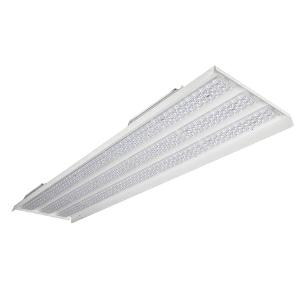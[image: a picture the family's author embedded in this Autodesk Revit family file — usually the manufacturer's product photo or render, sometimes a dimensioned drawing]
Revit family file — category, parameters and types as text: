
# Revit family: 3f_filippi_-_kit_led_retrofit_beta_430_3x_3f_filippi_-_a5311_a5322_-_kit_led_beta_430_-_l1551-_3x65w_ampio___vs_731e
name_source: partatom
category: Lighting Fixtures
units: mm (PartAtom-declared; Revit-internal decimal feet)

## family parameters
Cut with Voids When Loaded = No
Host = Face
Light Source = No
Part Type = Normal
Room Calculation Point = No
Round Connector Dimension = Use Diameter
Shared = No

## types (1)
- 3F Filippi - Kit LED Retrofit Beta 430 3X (1 x LED, 25759 lm, 173 W, 4000 K)
    Apparent Load = 173 VA
    Approval mark = ENEC
    CIE Flux Codes = 67 92 98 100 100
    Color Rendering = 80
    Color Temperature = 4000 K
    Control Gear = Electronic ballast
    Default Elevation = 1800 mm
    Description = Beta 430 Retrofit Kit to replace the 4x80W T5 Amalgam version

ILLUMINOTECHNICAL
Luminous efficiency 100% (DLOR 100%, ULOR 0%).
Initial luminous flux of the luminaire 25759 lm.
Wide symmetric distribution.
Installation Interdistance Transv.D = 1.36 x hu - Long.D = 1.35 x hu.
Tabular UGR (CIE 117 - 4H-8H; S=0.25H; 70/50/20): RUG 20.8 - 21.3.
Beam angle: 88° - 89°.
Luminous efficacy 149 lm/W.
Lifetime (L93/B10): 30000 h. (tq+25°C)
Lifetime (L90/B10): 50000 h. (tq+25°C)
Lifetime (L85/B10): 80000 h. (tq+25°C)
Lifetime (L80/B10): 100000 h. (tq+25°C)
Lifetime (L85/B10): 50000 h. (tq+40°C)
Sudden decreased luminous flux after 50000 hours: 0% (C0).
Photobiological safety in compliance with IEC/TR 62778: RG0 risk exempt, (IEC 62471).
In compliance with IEC/EN 62722-2-1 - IEC/EN 62717 standards.

SOURCE
3 linear LED modules 65W/840.
Energy efficiency class (UE 2019/2020 - UE 2019/2015): C.
CIE 13.3 Colour rendering index: CRI >80 (R9 <50%).
IES TM-30 Fidelity Index: Rf = 84 Rg = 95.
CCT nominal colour temperature 4000 K.
Colour initial tolerance (MacAdam): SDCM 3.

MECHANICAL
Gear-tray unit hot-galvanised steel, painted in white polyester.
Methacrylate (PMMA) lenses with external flat surface.
Luminaire with limited surface temperature. - D - (EN 60598-2-24)
Dimensions: 1551x430 mm, height 159 mm. Weight 13.875 kg.
Mechanical strength to impacts IK08 (5 joule).
Glow-wire test resistance 850°C.

ELECTRICAL
Halogen Free electronic wiring 230V-50/60Hz, power factor 0.97, THD <25%, constant output current, class I, 2 driver.
Twin-circuit.
Power of the luminaire 173 W.
CE - IEC 60598-1 - EN 60598-1.
SAFE FLICKER: PstLM=<1 and SVM=<0.4 (IEC TR 61547-1 and IEC TR 63158), to ensure a more comfortable and safe light.
Luminaire compliant with EN 60598-2-22 for power supply from a centralised emergency system CPSS (Central Power Supply System), not incorporated in the luminaire - high risk areas excluded. The default power and flux are 100% in AC and 100% in DC.
Ambient temperature from -20°C to +40°C.
Temperature class T6 max 85°C.
Relative humidity UR: <85%.

INSTALLATION
Retrofit.
Correct installation of the retrofit LED kit, compliant with EN 60598-1 and CE marked, inside the 3F Filippi - Beta 4x and 6x i3F 76 Fluorescent luminaires must be only carried out by qualified personnel to ensure compliance with the national installation standards.
Attention: to maintain the degree of protection of the device and for the purposes of validity of the guarantee of the new retrofit kits, it is imperative to replace the old cable guides (on the body of the device) with the new ones supplied.
All accessories dedicated to this product are available on the Catalog and on our website www.3F-Filippi.com.

ACCESSORIES
A5322 - Printed glass with Beta 430 frame - L1551.

WARNING
Fixture not suitable for cold stores with an ambient temperature <0°C and/or relative humidity >85%.
Luminaire designed for disposal/recycling at end-of-life.
Replaceable (LED only) light source by a professional. Replaceable control gear by a professional.
    Height = 159 mm
    Lamp = 1 x LED
    Lamp Light Flux = 25759 lm
    Lamp Power = 173 W
    Lamp count = 1
    Length = 1551 mm
    Lifetime = 50000 h
    Luminous efficacy = 149 lm/W
    Manufacturer = 3F Filippi
    ModVariant = No
    Model = 3F Filippi - A5311+A5322 - Kit LED Beta 430 - L1551- 3X65W AMPIO + VS
    Mounting Place = Ceiling
    Mounting Type = Surface mounted
    Number of Poles = 1
    OnlyDefault = Yes
    Power Factor = 1
    Product Name = 3F Filippi - Kit LED Retrofit Beta 430 3X
    Product group = ceiling mounted luminaire
    ProductGroupID = 3
    Protection Class = Protection class I
    Protection Degree = Degree of protection
    RLX_Detail_Level = 1
    RLX_Emergency_Light_Flux = 0 lm
    RLX_Emergency_Type = 0
    RLX_Emergency_Type_DB = No
    RlxData = <blob elided: 58913 chars, md5=22467619>
    Socket = socket
    Standby Power = 0 W
    System Light Flux = 25760 lm
    System Power = 173 W
    Type Comments = Product without accessories
    Type Image = 3ffilippi_a5311_a5322.jpg
    URL = http://relux.com
    VarID = ---
    Voltage = 0 V
    Weight = 0.00 kg
    Width = 430 mm

## geometry (parser evidence)
native form markers: Blend x4, Sweep x11
no freeform markers — native parametric forms only
